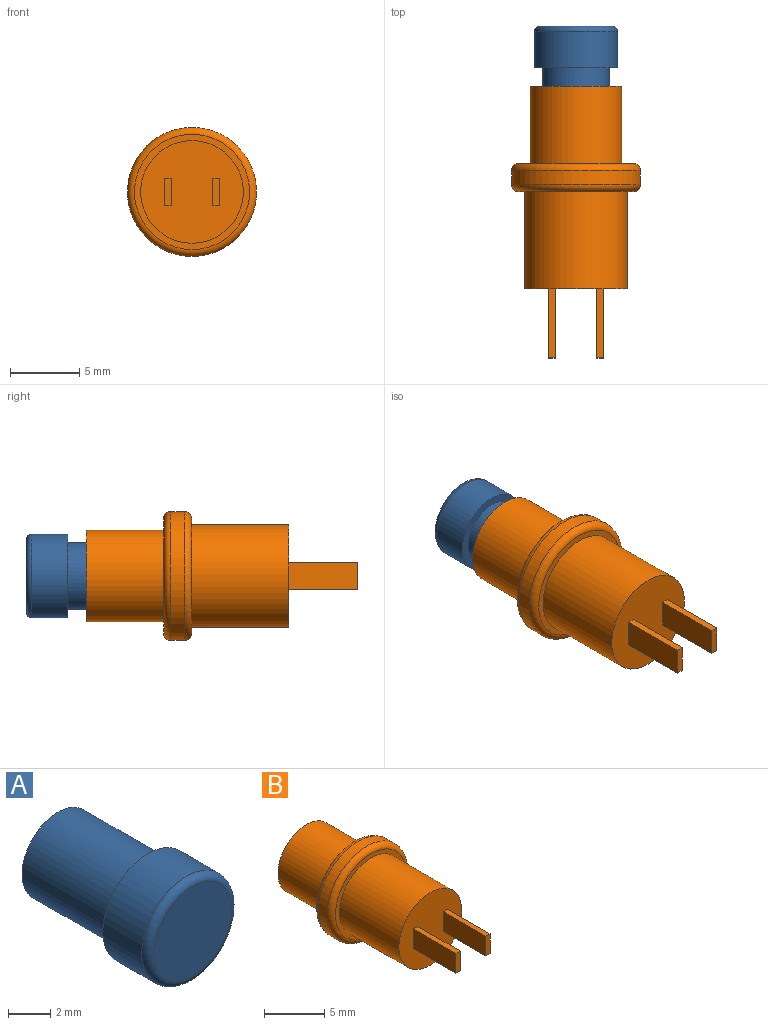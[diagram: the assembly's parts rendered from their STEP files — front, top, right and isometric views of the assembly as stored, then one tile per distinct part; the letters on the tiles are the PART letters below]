
ASSEMBLY  parts=2 mates=1
PART A: 6 faces, bbox 6.5x9x6.5 mm
  f0: cylinder r=2.4mm len=6mm, axis (0,-1,0), area 90.5mm2, adj f1,f4
  f1: plane 4.8x4.8mm, normal (0,1,0), area 18.1mm2, adj f0
  f2: cylinder r=3mm len=6mm, axis (0,1,0), area 49mm2, adj f4,f5
  f3: plane 5.2x5.2mm, normal (0,-1,0), area 21.2mm2, adj f5
  f4: plane 6x6mm, normal (0,1,0), area 10.2mm2, adj f0,f2
  f5: torus R=2.6mm, axis (0,-1,0), area 11.3mm2, adj f2,f3
PART B: 21 faces, bbox 10.1x19.6x10.1 mm
  f0: plane 7.4x7.4mm, normal (0,-1,0), area 41mm2, adj f9,f11,f12,f13,f14,f16,f17,f18
  f1: cylinder r=2.4mm len=7.6mm, axis (0,1,0), area 114.6mm2, adj f3,f10
  f2: cylinder r=3.3mm len=6.6mm, axis (0,1,0), area 116.1mm2, adj f3,f6
  f3: plane 6.6x6.6mm, normal (0,1,0), area 16.1mm2, adj f1,f2
  f4: cylinder r=4.65mm len=9.3mm, axis (0,1,0), area 29.2mm2, adj f7,f8
  f5: plane 8.3x8.3mm, normal (0,-1,0), area 11.1mm2, adj f8,f9
  f6: plane 8.3x8.3mm, normal (0,1,0), area 19.9mm2, adj f2,f7
  f7: torus R=4.15mm, axis (0,-1,0), area 22.1mm2, adj f4,f6
  f8: torus R=4.15mm, axis (0,-1,0), area 22.1mm2, adj f4,f5
  f9: cylinder r=3.7mm len=7.4mm, axis (0,1,0), area 162.7mm2, adj f0,f5
  f10: plane 4.8x4.8mm, normal (0,1,0), area 18.1mm2, adj f1
  f11: plane 5x0.5mm, normal (0,0,1), area 2.5mm2, adj f0,f12,f14,f15
  f12: plane 5x2mm, normal (-1,0,0), area 10mm2, adj f0,f11,f13,f15
  f13: plane 5x0.5mm, normal (0,0,-1), area 2.5mm2, adj f0,f12,f14,f15
  f14: plane 5x2mm, normal (1,0,0), area 10mm2, adj f0,f11,f13,f15
  f15: plane 2x0.5mm, normal (0,-1,0), area 1mm2, adj f11,f12,f13,f14
  f16: plane 5x0.5mm, normal (0,0,1), area 2.5mm2, adj f0,f17,f19,f20
  f17: plane 5x2mm, normal (-1,0,0), area 10mm2, adj f0,f16,f18,f20
  f18: plane 5x0.5mm, normal (0,0,-1), area 2.5mm2, adj f0,f17,f19,f20
  f19: plane 5x2mm, normal (1,0,0), area 10mm2, adj f0,f16,f18,f20
  f20: plane 2x0.5mm, normal (0,-1,0), area 1mm2, adj f16,f17,f18,f19
PLACE A rot(axis=(0,0,1),180deg) t=(0,1.33,0)mm
PLACE B at identity fixed
MATE slider B.f1 <-> A.f0  axis (0,1,0) through (0,0,0)mm
